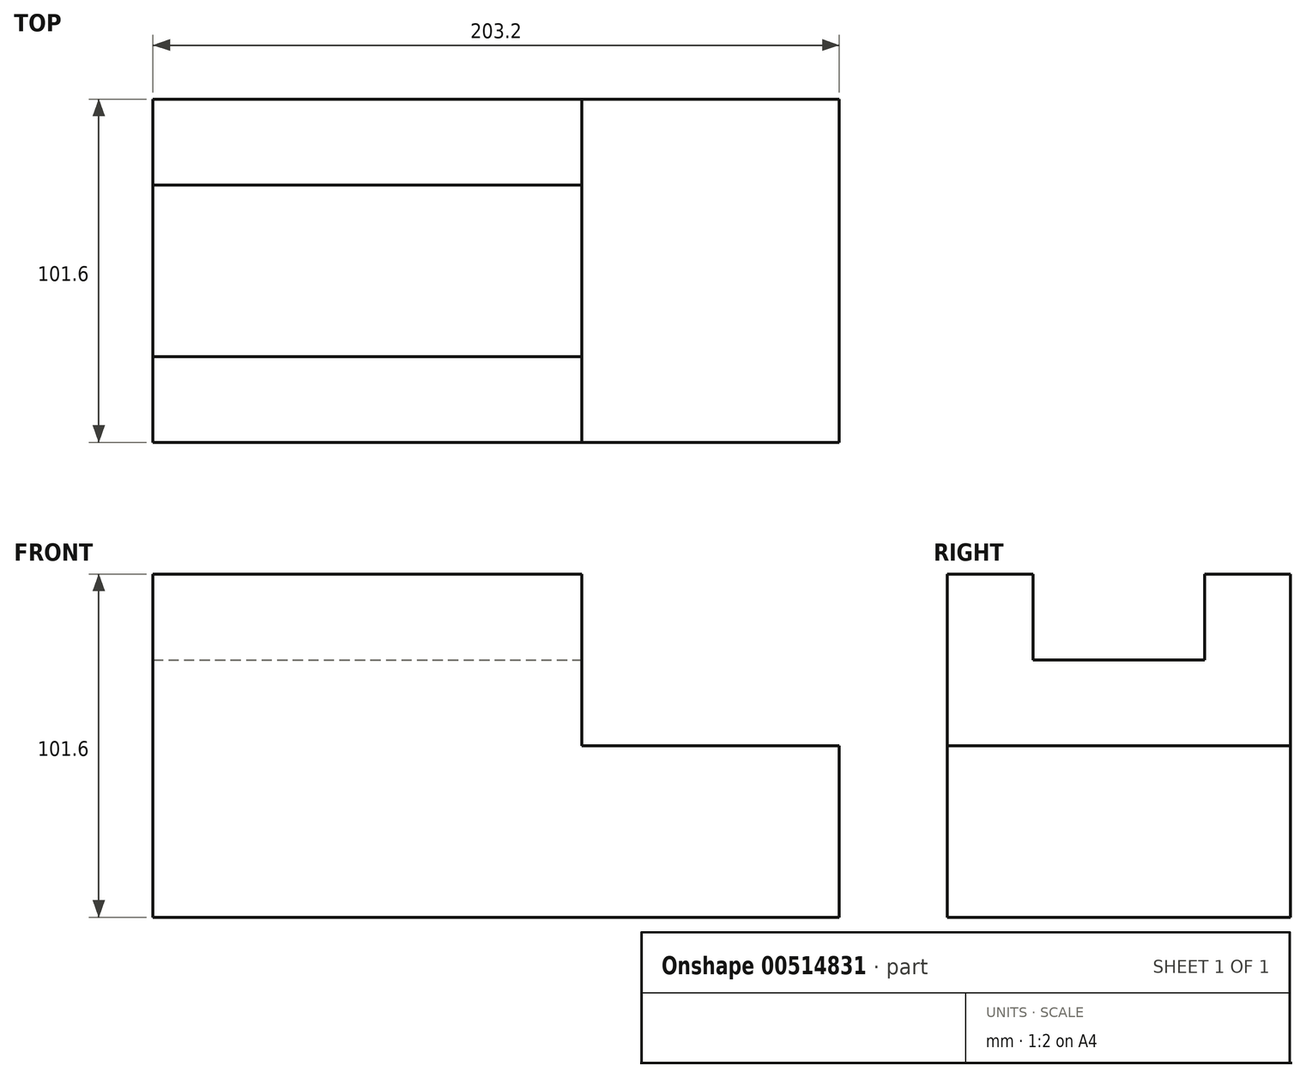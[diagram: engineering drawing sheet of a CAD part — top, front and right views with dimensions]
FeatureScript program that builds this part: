
annotation { "Feature Type Name" : "Feature", "Feature Type Description" : "" }
export const myFeature = defineFeature(function(context is Context, id is Id, definition is map)
    precondition{}
    {
        {
            var Q0;
            Q0=qCreatedBy(makeId("Top.planeOp"),FACE);
            var sketch = newSketch(context, id + "F0", { "sketchPlane" : qUnion([Q0])});
            skLineSegment(sketch, "E0.bottom", {"start": v(-115.57, 19.19) * mm, "end": v(87.63, 19.19) * mm});
            skLineSegment(sketch, "E0.top", {"start": v(-115.57, -82.41) * mm, "end": v(87.63, -82.41) * mm});
            skLineSegment(sketch, "E0.left", {"start": v(-115.57, 19.19) * mm, "end": v(-115.57, -6.21) * mm});
            skLineSegment(sketch, "E0.right", {"start": v(87.63, 19.19) * mm, "end": v(87.63, -82.41) * mm});
            skLineSegment(sketch, "E1", {"start": v(-115.57, -6.21) * mm, "end": v(-115.57, -57.01) * mm});
            skLineSegment(sketch, "E2", {"start": v(-115.57, -57.01) * mm, "end": v(-115.57, -82.41) * mm});
            skSolve(sketch);
        }
        {
            var Q0;
            Q0=makeQuery(id+"F0.imprint","IMPRINT",FACE,{"disambiguationData":[TD([[makeQuery(id+"F0.imprint","IMPRINT",EDGE,{"derivedFrom":sQuery(id+"F0.wireOp",EDGE,"E0.bottom")}),-1.0]])]});
            extrude(context, id + "F1", {"entities" : qUnion([Q0]), "depth" : 101.6 * mm, "offsetDistance" : 25.4 * mm});
        }
        {
            var Q0;
            Q0=makeQuery(id+"F1.opExtrude","CAP_FACE",FACE,{"disambiguationData":[OSD([sQuery(id+"F0.wireOp",EDGE,"E0.bottom"),sQuery(id+"F0.wireOp",EDGE,"E0.top"),sQuery(id+"F0.wireOp",EDGE,"E0.left"),sQuery(id+"F0.wireOp",EDGE,"E0.right")])],"isStart":false});
            var sketch = newSketch(context, id + "F2", { "sketchPlane" : qUnion([Q0])});
            skLineSegment(sketch, "E3.bottom", {"start": v(11.43, 19.19) * mm, "end": v(87.63, 19.19) * mm});
            skLineSegment(sketch, "E3.top", {"start": v(11.43, -82.41) * mm, "end": v(87.63, -82.41) * mm});
            skLineSegment(sketch, "E3.left", {"start": v(11.43, 19.19) * mm, "end": v(11.43, -82.41) * mm});
            skLineSegment(sketch, "E3.right", {"start": v(87.63, 19.19) * mm, "end": v(87.63, -82.41) * mm});
            skSolve(sketch);
        }
        {
            var Q0;
            Q0=makeQuery(id+"F2.imprint","IMPRINT",FACE,{"disambiguationData":[TD([[makeQuery(id+"F2.imprint","IMPRINT",EDGE,{"derivedFrom":sQuery(id+"F2.wireOp",EDGE,"E3.bottom")}),-1.0]])]});
            extrude(context, id + "F3", {"entities" : qUnion([Q0]), "operationType" : NewBodyOperationType.REMOVE, "oppositeDirection" : true, "depth" : 50.8 * mm, "offsetDistance" : 25.4 * mm});
        }
        {
            var Q0;
            Q0=makeQuery(id+"F1.opExtrude","CAP_FACE",FACE,{"disambiguationData":[OSD([sQuery(id+"F0.wireOp",EDGE,"E0.bottom"),sQuery(id+"F0.wireOp",EDGE,"E0.top"),sQuery(id+"F0.wireOp",EDGE,"E0.left"),sQuery(id+"F0.wireOp",EDGE,"E0.right"),sQuery(id+"F0.wireOp",EDGE,"E1"),sQuery(id+"F0.wireOp",EDGE,"E2")])],"isStart":false});
            var sketch = newSketch(context, id + "F4", { "sketchPlane" : qUnion([Q0])});
            skLineSegment(sketch, "E4.bottom", {"start": v(-115.57, -6.21) * mm, "end": v(17.15, -6.21) * mm});
            skLineSegment(sketch, "E4.top", {"start": v(-115.57, -57.01) * mm, "end": v(17.15, -57.01) * mm});
            skLineSegment(sketch, "E4.left", {"start": v(-115.57, -6.21) * mm, "end": v(-115.57, -57.01) * mm});
            skLineSegment(sketch, "E4.right", {"start": v(17.15, -6.21) * mm, "end": v(17.15, -57.01) * mm});
            skSolve(sketch);
        }
        {
            var Q0;
            Q0 = qSketchRegion(id + "F4", true);
            extrude(context, id + "F5", {"entities" : qUnion([Q0]), "operationType" : NewBodyOperationType.REMOVE, "oppositeDirection" : true, "depth" : 25.4 * mm, "offsetDistance" : 25.4 * mm});
        }
    });
